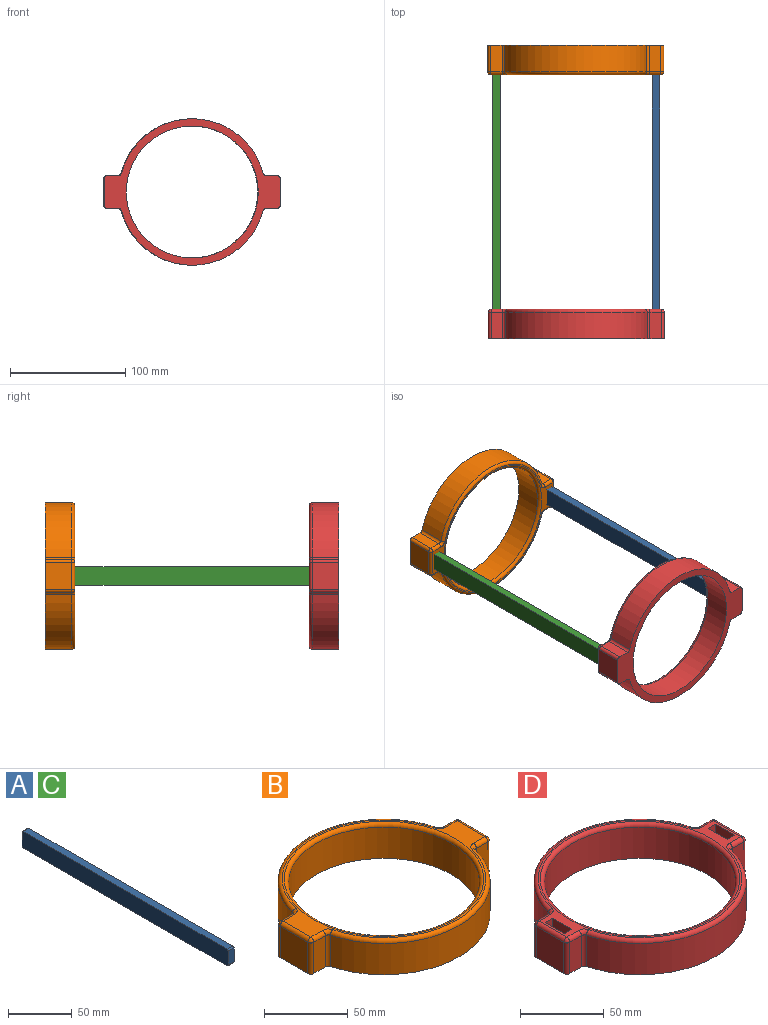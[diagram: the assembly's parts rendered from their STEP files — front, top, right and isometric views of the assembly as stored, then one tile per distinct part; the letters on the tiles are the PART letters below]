
ASSEMBLY  parts=4 mates=3
PART A: 10 faces, bbox 6.4x228.6x15.9 mm
  f0: plane 228.6x15.88mm, normal (1,0,0), area 3627.6mm2, adj f1,f3,f4,f5,f6,f7,f8,f9
  f1: plane 226.06x6.35mm, normal (0,0,1), area 1435.5mm2, adj f0,f2,f6,f8
  f2: plane 228.6x15.88mm, normal (-1,0,0), area 3627.6mm2, adj f1,f3,f4,f5,f6,f7,f8,f9
  f3: plane 226.06x6.35mm, normal (0,0,-1), area 1435.5mm2, adj f0,f2,f7,f9
  f4: plane 13.34x6.35mm, normal (0,-1,0), area 84.7mm2, adj f0,f2,f8,f9
  f5: plane 13.34x6.35mm, normal (0,1,0), area 84.7mm2, adj f0,f2,f6,f7
  f6: cylinder r=1.27mm len=6.35mm, axis (-1,0,0), area 12.7mm2, adj f0,f1,f2,f5
  f7: cylinder r=1.27mm len=6.35mm, axis (1,0,0), area 12.7mm2, adj f0,f2,f3,f5
  f8: cylinder r=1.27mm len=6.35mm, axis (1,0,0), area 12.7mm2, adj f0,f1,f2,f4
  f9: cylinder r=1.27mm len=6.35mm, axis (-1,0,0), area 12.7mm2, adj f0,f2,f3,f4
PART B: 50 faces, bbox 152.4x137.5x25.4 mm
  f0: plane 152.4x127mm, normal (0,0,-1), area 2948mm2, adj f2,f3,f4,f5,f6,f7,f8,f9
  f1: plane 147.32x121.92mm, normal (0,0,1), area 1108.4mm2, adj f12,f14,f15,f18,f20,f21,f26,f27
  f2: plane 22.86x9.8mm, normal (0,-1,0), area 224mm2, adj f0,f16,f21,f22
  f3: cylinder r=63.5mm len=122.81mm, axis (0,0,-1), area 3812.4mm2, adj f0,f11,f15,f16
  f4: plane 22.86x9.8mm, normal (0,-1,0), area 224mm2, adj f0,f11,f13,f14
  f5: plane 23.5x22.86mm, normal (1,0,0), area 537.1mm2, adj f0,f13,f19,f20
  f6: plane 22.86x9.8mm, normal (0,1,0), area 224mm2, adj f0,f19,f25,f26
  f7: cylinder r=63.5mm len=122.81mm, axis (0,0,-1), area 3812.4mm2, adj f0,f25,f31,f34
  f8: plane 22.86x9.8mm, normal (0,1,0), area 224mm2, adj f0,f28,f32,f34
  f9: plane 23.5x22.86mm, normal (-1,0,0), area 537.1mm2, adj f0,f22,f27,f28
  f10: cylinder r=57.15mm len=114.3mm, axis (0,0,-1), area 8208.7mm2, adj f0,f35
  f11: cylinder r=2.54mm len=22.86mm, axis (0,0,-1), area 76.2mm2, adj f0,f3,f4,f12
  f12: torus R=5.08mm, axis (0,0,1), area 18.1mm2, adj f1,f11,f14,f15
  f13: cylinder r=2.54mm len=22.86mm, axis (0,0,-1), area 91.2mm2, adj f0,f4,f5,f17
  f14: cylinder r=2.54mm len=9.8mm, axis (-1,0,0), area 39.1mm2, adj f1,f4,f12,f17
  f15: torus R=60.96mm, axis (0,0,1), area 655.7mm2, adj f1,f3,f12,f18
  f16: cylinder r=2.54mm len=22.86mm, axis (0,0,-1), area 76.2mm2, adj f0,f2,f3,f18
  f17: sphere r=2.54mm, area 10.1mm2, adj f13,f14,f20
  f18: torus R=5.08mm, axis (0,0,1), area 18.1mm2, adj f1,f15,f16,f21
  f19: cylinder r=2.54mm len=22.86mm, axis (0,0,1), area 91.2mm2, adj f0,f5,f6,f23
  f20: cylinder r=2.54mm len=23.5mm, axis (0,-1,0), area 93.7mm2, adj f1,f5,f17,f23
  f21: cylinder r=2.54mm len=9.8mm, axis (-1,0,0), area 39.1mm2, adj f1,f2,f18,f24
  f22: cylinder r=2.54mm len=22.86mm, axis (0,0,1), area 91.2mm2, adj f0,f2,f9,f24
  f23: sphere r=2.54mm, area 10.1mm2, adj f19,f20,f26
  f24: sphere r=2.54mm, area 10.1mm2, adj f21,f22,f27
  f25: cylinder r=2.54mm len=22.86mm, axis (0,0,-1), area 76.2mm2, adj f0,f6,f7,f29
  f26: cylinder r=2.54mm len=9.8mm, axis (1,0,0), area 39.1mm2, adj f1,f6,f23,f29
  f27: cylinder r=2.54mm len=23.5mm, axis (0,1,0), area 93.7mm2, adj f1,f9,f24,f30
  f28: cylinder r=2.54mm len=22.86mm, axis (0,0,-1), area 91.2mm2, adj f0,f8,f9,f30
  f29: torus R=5.08mm, axis (0,0,1), area 18.1mm2, adj f1,f25,f26,f31
  f30: sphere r=2.54mm, area 10.1mm2, adj f27,f28,f32
  f31: torus R=60.96mm, axis (0,0,1), area 655.7mm2, adj f1,f7,f29,f33
  f32: cylinder r=2.54mm len=9.8mm, axis (1,0,0), area 39.1mm2, adj f1,f8,f30,f33
  f33: torus R=5.08mm, axis (0,0,1), area 18.1mm2, adj f1,f31,f32,f34
  f34: cylinder r=2.54mm len=22.86mm, axis (0,0,-1), area 76.2mm2, adj f0,f7,f8,f33
  f35: torus R=59.69mm, axis (0,0,1), area 1455.8mm2, adj f1,f10
  f36: plane 19.05x16.13mm, normal (1,0,0), area 306.6mm2, adj f0,f37,f39,f40,f46,f47
  f37: plane 17.78x6.6mm, normal (0,1,0), area 117.4mm2, adj f0,f36,f38,f46
  f38: plane 19.05x16.13mm, normal (-1,0,0), area 306.6mm2, adj f0,f37,f39,f40,f46,f47
  f39: plane 17.78x6.6mm, normal (0,-1,0), area 117.4mm2, adj f0,f36,f38,f47
  f40: plane 13.59x6.6mm, normal (0,0,-1), area 89.7mm2, adj f36,f38,f46,f47
  f41: plane 19.05x16.13mm, normal (-1,0,0), area 306.6mm2, adj f0,f42,f44,f45,f48,f49
  f42: plane 17.78x6.6mm, normal (0,-1,0), area 117.4mm2, adj f0,f41,f43,f48
  f43: plane 19.05x16.13mm, normal (1,0,0), area 306.6mm2, adj f0,f42,f44,f45,f48,f49
  f44: plane 17.78x6.6mm, normal (0,1,0), area 117.4mm2, adj f0,f41,f43,f49
  f45: plane 13.59x6.6mm, normal (0,0,-1), area 89.7mm2, adj f41,f43,f48,f49
  f46: cylinder r=1.27mm len=6.6mm, axis (1,0,0), area 13.2mm2, adj f36,f37,f38,f40
  f47: cylinder r=1.27mm len=6.6mm, axis (-1,0,0), area 13.2mm2, adj f36,f38,f39,f40
  f48: cylinder r=1.27mm len=6.6mm, axis (-1,0,0), area 13.2mm2, adj f41,f42,f43,f45
  f49: cylinder r=1.27mm len=6.6mm, axis (1,0,0), area 13.2mm2, adj f41,f43,f44,f45
PART C: same geometry as A
PART D: 50 faces, bbox 152.4x137.5x25.4 mm
  f0: plane 147.32x121.92mm, normal (0,0,1), area 895.4mm2, adj f11,f12,f13,f14,f16,f17,f18,f19
  f1: plane 22.86x9.8mm, normal (0,-1,0), area 224mm2, adj f10,f26,f31,f32
  f2: cylinder r=63.5mm len=122.81mm, axis (0,0,1), area 3812.4mm2, adj f10,f21,f25,f26
  f3: plane 22.86x9.8mm, normal (0,-1,0), area 224mm2, adj f10,f21,f23,f24
  f4: plane 23.5x22.86mm, normal (1,0,0), area 537.1mm2, adj f10,f23,f29,f30
  f5: plane 22.86x9.8mm, normal (0,1,0), area 224mm2, adj f10,f29,f35,f36
  f6: cylinder r=63.5mm len=122.81mm, axis (0,0,1), area 3812.4mm2, adj f10,f35,f41,f44
  f7: plane 22.86x9.8mm, normal (0,1,0), area 224mm2, adj f10,f38,f42,f44
  f8: plane 23.5x22.86mm, normal (-1,0,0), area 537.1mm2, adj f10,f32,f37,f38
  f9: cylinder r=57.15mm len=114.3mm, axis (0,0,1), area 8208.7mm2, adj f10,f45
  f10: plane 152.4x127mm, normal (0,0,-1), area 3161mm2, adj f1,f2,f3,f4,f5,f6,f7,f8
  f11: plane 19.05x16.13mm, normal (1,0,0), area 306.6mm2, adj f0,f12,f14,f15,f46,f47
  f12: plane 17.78x6.6mm, normal (0,1,0), area 117.4mm2, adj f0,f11,f13,f46
  f13: plane 19.05x16.13mm, normal (-1,0,0), area 306.6mm2, adj f0,f12,f14,f15,f46,f47
  f14: plane 17.78x6.6mm, normal (0,-1,0), area 117.4mm2, adj f0,f11,f13,f47
  f15: plane 13.59x6.6mm, normal (0,0,1), area 89.7mm2, adj f11,f13,f46,f47
  f16: plane 19.05x16.13mm, normal (-1,0,0), area 306.6mm2, adj f0,f17,f19,f20,f48,f49
  f17: plane 17.78x6.6mm, normal (0,-1,0), area 117.4mm2, adj f0,f16,f18,f48
  f18: plane 19.05x16.13mm, normal (1,0,0), area 306.6mm2, adj f0,f17,f19,f20,f48,f49
  f19: plane 17.78x6.6mm, normal (0,1,0), area 117.4mm2, adj f0,f16,f18,f49
  f20: plane 13.59x6.6mm, normal (0,0,1), area 89.7mm2, adj f16,f18,f48,f49
  f21: cylinder r=2.54mm len=22.86mm, axis (0,0,1), area 76.2mm2, adj f2,f3,f10,f22
  f22: torus R=5.08mm, axis (0,0,1), area 18.1mm2, adj f0,f21,f24,f25
  f23: cylinder r=2.54mm len=22.86mm, axis (0,0,1), area 91.2mm2, adj f3,f4,f10,f27
  f24: cylinder r=2.54mm len=9.8mm, axis (1,0,0), area 39.1mm2, adj f0,f3,f22,f27
  f25: torus R=60.96mm, axis (0,0,1), area 655.7mm2, adj f0,f2,f22,f28
  f26: cylinder r=2.54mm len=22.86mm, axis (0,0,1), area 76.2mm2, adj f1,f2,f10,f28
  f27: sphere r=2.54mm, area 10.1mm2, adj f23,f24,f30
  f28: torus R=5.08mm, axis (0,0,1), area 18.1mm2, adj f0,f25,f26,f31
  f29: cylinder r=2.54mm len=22.86mm, axis (0,0,-1), area 91.2mm2, adj f4,f5,f10,f33
  f30: cylinder r=2.54mm len=23.5mm, axis (0,1,0), area 93.7mm2, adj f0,f4,f27,f33
  f31: cylinder r=2.54mm len=9.8mm, axis (1,0,0), area 39.1mm2, adj f0,f1,f28,f34
  f32: cylinder r=2.54mm len=22.86mm, axis (0,0,-1), area 91.2mm2, adj f1,f8,f10,f34
  f33: sphere r=2.54mm, area 10.1mm2, adj f29,f30,f36
  f34: sphere r=2.54mm, area 10.1mm2, adj f31,f32,f37
  f35: cylinder r=2.54mm len=22.86mm, axis (0,0,1), area 76.2mm2, adj f5,f6,f10,f39
  f36: cylinder r=2.54mm len=9.8mm, axis (-1,0,0), area 39.1mm2, adj f0,f5,f33,f39
  f37: cylinder r=2.54mm len=23.5mm, axis (0,-1,0), area 93.7mm2, adj f0,f8,f34,f40
  f38: cylinder r=2.54mm len=22.86mm, axis (0,0,1), area 91.2mm2, adj f7,f8,f10,f40
  f39: torus R=5.08mm, axis (0,0,1), area 18.1mm2, adj f0,f35,f36,f41
  f40: sphere r=2.54mm, area 10.1mm2, adj f37,f38,f42
  f41: torus R=60.96mm, axis (0,0,1), area 655.7mm2, adj f0,f6,f39,f43
  f42: cylinder r=2.54mm len=9.8mm, axis (-1,0,0), area 39.1mm2, adj f0,f7,f40,f43
  f43: torus R=5.08mm, axis (0,0,1), area 18.1mm2, adj f0,f41,f42,f44
  f44: cylinder r=2.54mm len=22.86mm, axis (0,0,1), area 76.2mm2, adj f6,f7,f10,f43
  f45: torus R=59.69mm, axis (0,0,1), area 1455.8mm2, adj f0,f9
  f46: cylinder r=1.27mm len=6.6mm, axis (1,0,0), area 13.2mm2, adj f11,f12,f13,f15
  f47: cylinder r=1.27mm len=6.6mm, axis (-1,0,0), area 13.2mm2, adj f11,f13,f14,f15
  f48: cylinder r=1.27mm len=6.6mm, axis (-1,0,0), area 13.2mm2, adj f16,f17,f18,f20
  f49: cylinder r=1.27mm len=6.6mm, axis (1,0,0), area 13.2mm2, adj f16,f18,f19,f20
PLACE A t=(-98.23,-79.35,-33.96)mm
PLACE B rot(axis=(1,0,0),90deg) t=(-167.61,54,-33.96)mm
PLACE C t=(-236.15,-79.35,-33.96)mm
PLACE D rot(axis=(-1,0,0),90deg) t=(-167.19,-174.6,-33.96)mm
MATE fastened D.f20 <-> C.f4  axis (0,1,0) through (-236.15,-193.65,-33.96)mm
MATE fastened C.f5 <-> B.f45  axis (0,1,0) through (-236.15,34.95,-33.96)mm
MATE fastened D.f15 <-> A.f4  axis (0,1,0) through (-98.23,-193.65,-33.96)mm
